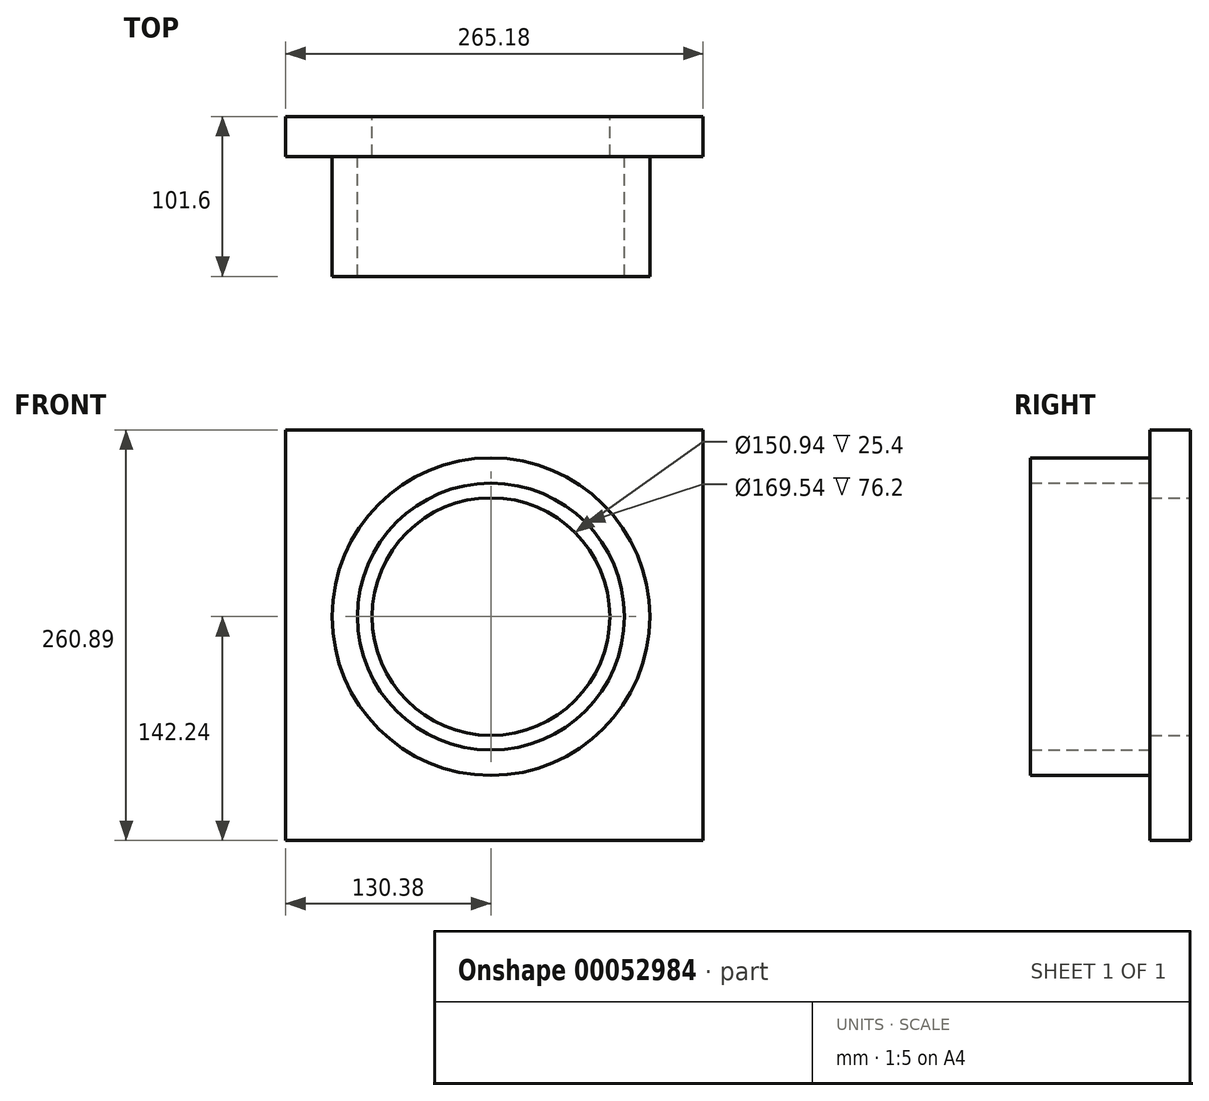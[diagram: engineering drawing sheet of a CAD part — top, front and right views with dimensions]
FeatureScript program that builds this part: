
annotation { "Feature Type Name" : "Feature", "Feature Type Description" : "" }
export const myFeature = defineFeature(function(context is Context, id is Id, definition is map)
    precondition{}
    {
        {
            var Q0;
            Q0=qCreatedBy(makeId("Front.planeOp"),FACE);
            var sketch = newSketch(context, id + "F0", { "sketchPlane" : qUnion([Q0])});
            skLineSegment(sketch, "E0.bottom", {"start": v(-130.38, 118.65) * mm, "end": v(134.8, 118.65) * mm});
            skLineSegment(sketch, "E0.top", {"start": v(-130.38, -142.24) * mm, "end": v(134.8, -142.24) * mm});
            skLineSegment(sketch, "E0.left", {"start": v(-130.38, 118.65) * mm, "end": v(-130.38, -142.24) * mm});
            skLineSegment(sketch, "E0.right", {"start": v(134.8, 118.65) * mm, "end": v(134.8, -142.24) * mm});
            skCircle(sketch, "E1", {"center": v(0, 0) * mm, "radius": 75.47 * mm});
            skSolve(sketch);
        }
        {
            var Q0;
            Q0 = qSketchRegion(id + "F0", true);
            extrude(context, id + "F1", {"entities" : qUnion([Q0]), "depth" : 25.4 * mm});
        }
        {
            var Q0;
            Q0=makeQuery(id+"F1.opExtrude","CAP_FACE",FACE,{"disambiguationData":[OSD([sQuery(id+"F0.wireOp",EDGE,"E0.bottom"),sQuery(id+"F0.wireOp",EDGE,"E0.top"),sQuery(id+"F0.wireOp",EDGE,"E0.left"),sQuery(id+"F0.wireOp",EDGE,"E0.right"),sQuery(id+"F0.wireOp",EDGE,"E1")])],"isStart":false});
            var sketch = newSketch(context, id + "F2", { "sketchPlane" : qUnion([Q0])});
            skCircle(sketch, "E2.0", {"center": v(0, 0) * mm, "radius": 75.47 * mm});
            skCircle(sketch, "E3.0", {"center": v(0, 0) * mm, "radius": 100.87 * mm});
            skLineSegment(sketch, "E4.0", {"start": v(-136.73, 118.65) * mm, "end": v(-136.73, -142.24) * mm});
            skCircle(sketch, "E5.0", {"center": v(0, 0) * mm, "radius": 84.77 * mm});
            skSolve(sketch);
        }
        {
            var Q0;
            Q0 = qSketchRegion(id + "F2", true);
            extrude(context, id + "F3", {"entities" : qUnion([Q0]), "operationType" : NewBodyOperationType.ADD, "depth" : 76.2 * mm});
        }
    });
